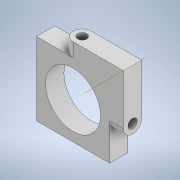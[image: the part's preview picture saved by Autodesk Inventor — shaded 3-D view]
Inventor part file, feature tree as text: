
AUTODESK INVENTOR PART (.ipt)
format: ipt  version: 2022.2 (Build 262287030, 287C)  size: 146,944 bytes
history: native  units: in
note: dims shown in document units (in); Inventor stores cm internally (conversion verified against a paired STEP export)
features: sketch x4, hole x3, extrude x2, plane x1, mirror x1
ambient origin geometry x8: Origin, YZ Plane, XZ Plane, XY Plane, X Axis, Y Axis, Z Axis, Center Point
bodies: Solid1 (feature_tree)
feature tree (11):
  extrude  "Extrusion1"  Depth=2.75in
  plane  "Work Plane1"
  mirror  "Mirror1"
  sketch  "Sketch3"  dims[d2=0.75in d3=0.0in d6=4.0in]
  extrude  "Extrusion2"  Depth=0.75in
  hole  "Hole1"  [1 undecoded]
  hole  "Hole2"  [1 undecoded]
  hole  "Hole3"  [1 undecoded]
  sketch  "Sketch2"  dims[d0=1.0in d1=2.75in]
  sketch  "Sketch4"  dims[d7=1.0in d8=0.0in]
  sketch  "Sketch5"  dims[d9=3.0in d10=0.75in d11=0.375in d12=0.25in d13=0.5635in d14=1.0in d15=0.8108in d16=0.5in d17=0.75in d18=0.375in d19=0.25in d20=0.5635in d21=1.0in d22=0.8108in d23=0.5in d24=0.75in d25=0.375in d26=0.25in d27=0.5635in d28=1.0in d29=0.8108in]
note: 3 required parameter values undecoded (feature->parameter linkage not recoverable at this tier; creation-order binding heuristic only, values carry confidence <= 0.55)
